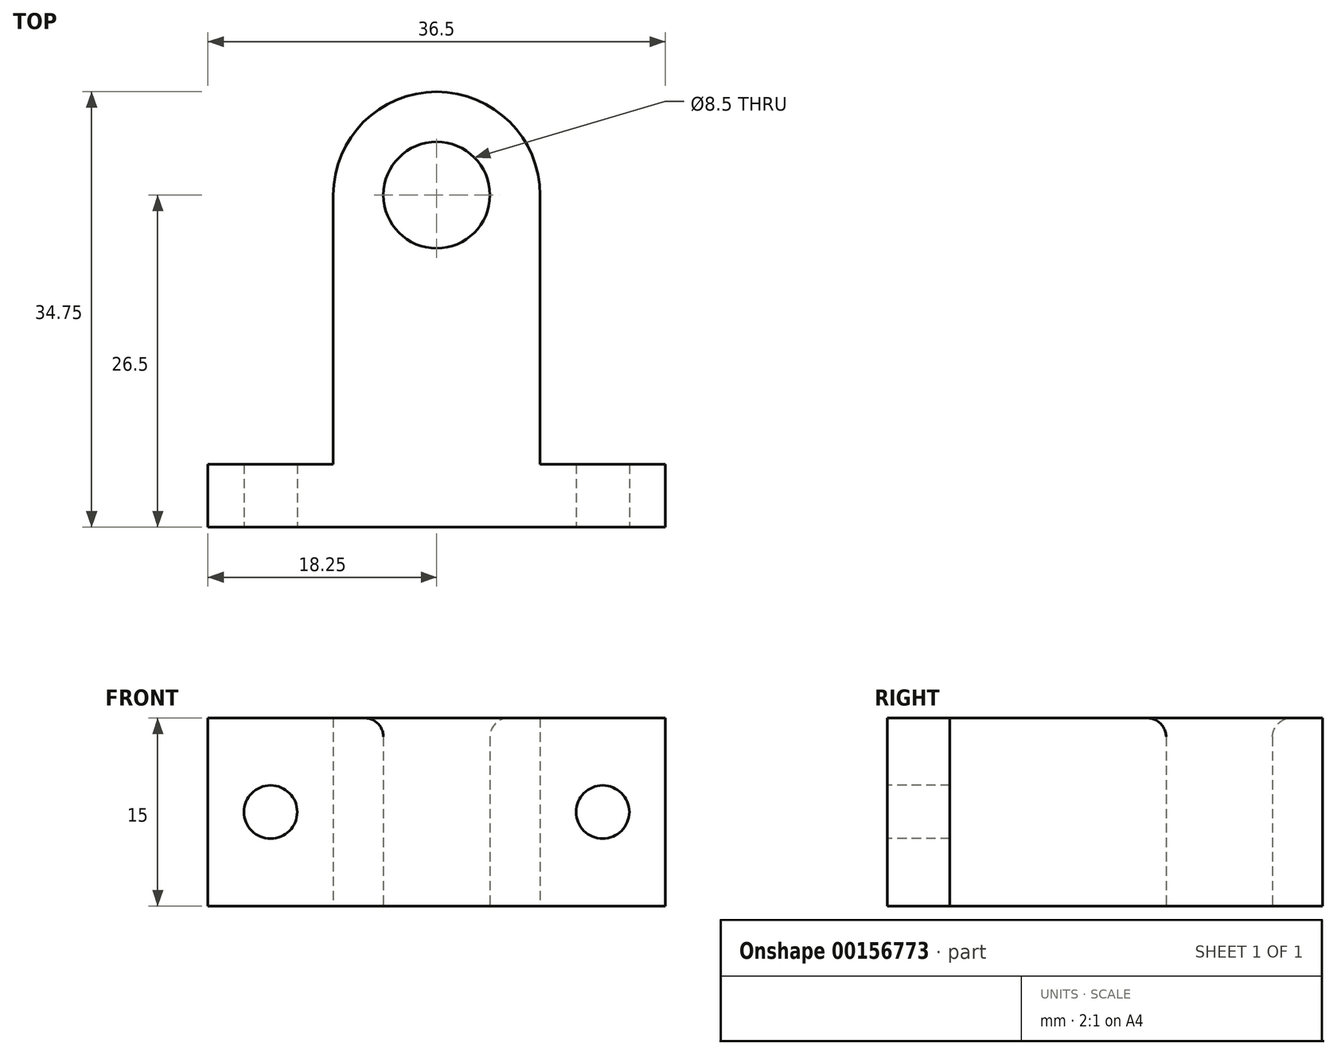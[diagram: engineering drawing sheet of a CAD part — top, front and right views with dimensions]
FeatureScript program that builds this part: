
annotation { "Feature Type Name" : "Feature", "Feature Type Description" : "" }
export const myFeature = defineFeature(function(context is Context, id is Id, definition is map)
    precondition{}
    {
        {
            var Q0;
            Q0=qCreatedBy(makeId("Top.planeOp"),FACE);
            var sketch = newSketch(context, id + "F0", { "sketchPlane" : qUnion([Q0])});
            skCircle(sketch, "E0", {"center": v(0, 0) * mm, "radius": 4.25 * mm});
            skArc(sketch, "E1", {"start": v(8.25, 0) * mm, "mid": v(0, 8.25) * mm, "end": v(-8.25, 0) * mm});
            skLineSegment(sketch, "E2", {"start": v(-8.25, 0) * mm, "end": v(-8.25, -21.5) * mm});
            skLineSegment(sketch, "E3", {"start": v(-8.25, -21.5) * mm, "end": v(-18.25, -21.5) * mm});
            skLineSegment(sketch, "E4", {"start": v(-18.25, -21.5) * mm, "end": v(-18.25, -26.5) * mm});
            skLineSegment(sketch, "E5", {"start": v(-18.25, -26.5) * mm, "end": v(0, -26.5) * mm});
            skLineSegment(sketch, "E6.MirrorCS", {"start": v(8.25, 0) * mm, "end": v(8.25, -21.5) * mm});
            skLineSegment(sketch, "E7.MirrorCS", {"start": v(8.25, -21.5) * mm, "end": v(18.25, -21.5) * mm});
            skLineSegment(sketch, "E8.MirrorCS", {"start": v(18.25, -21.5) * mm, "end": v(18.25, -26.5) * mm});
            skLineSegment(sketch, "E9.MirrorCS", {"start": v(18.25, -26.5) * mm, "end": v(0, -26.5) * mm});
            skSolve(sketch);
        }
        {
            var Q0;
            Q0=qSketchRegion(id+"F0",true);
            extrude(context, id + "F1", {"entities" : qUnion([Q0]), "depth" : 15 * mm});
        }
        {
            var Q0;
            Q0=makeQuery(id+"F1.opExtrude","SWEPT_FACE",FACE,{"disambiguationData":[OSD([sQuery(id+"F0.wireOp",EDGE,"E5"),sQuery(id+"F0.wireOp",EDGE,"E9.MirrorCS")])]});
            var sketch = newSketch(context, id + "F2", { "sketchPlane" : qUnion([Q0])});
            skCircle(sketch, "E10", {"center": v(-13.25, 7.5) * mm, "radius": 2.12 * mm});
            skCircle(sketch, "E11", {"center": v(13.25, 7.5) * mm, "radius": 2.12 * mm});
            skSolve(sketch);
        }
        {
            var Q0;
            Q0=qSketchRegion(id+"F2",true);
            extrude(context, id + "F3", {"entities" : qUnion([Q0]), "operationType" : NewBodyOperationType.REMOVE, "endBound" : BoundingType.THROUGH_ALL, "oppositeDirection" : true, "depth" : 25 * mm});
        }
        {
            var Q0;
            Q0=makeQuery(id+"F1.opExtrude","CAP_EDGE",EDGE,{"disambiguationData":[OSD([sQuery(id+"F0.wireOp",EDGE,"E0")])],"isStart":false});
            fillet(context, id + "F4", {"entities" : qUnion([Q0]), "radius" : 1.5 * mm, "tangentPropagation" : true, "allowEdgeOverflow" : false});
        }
    });
